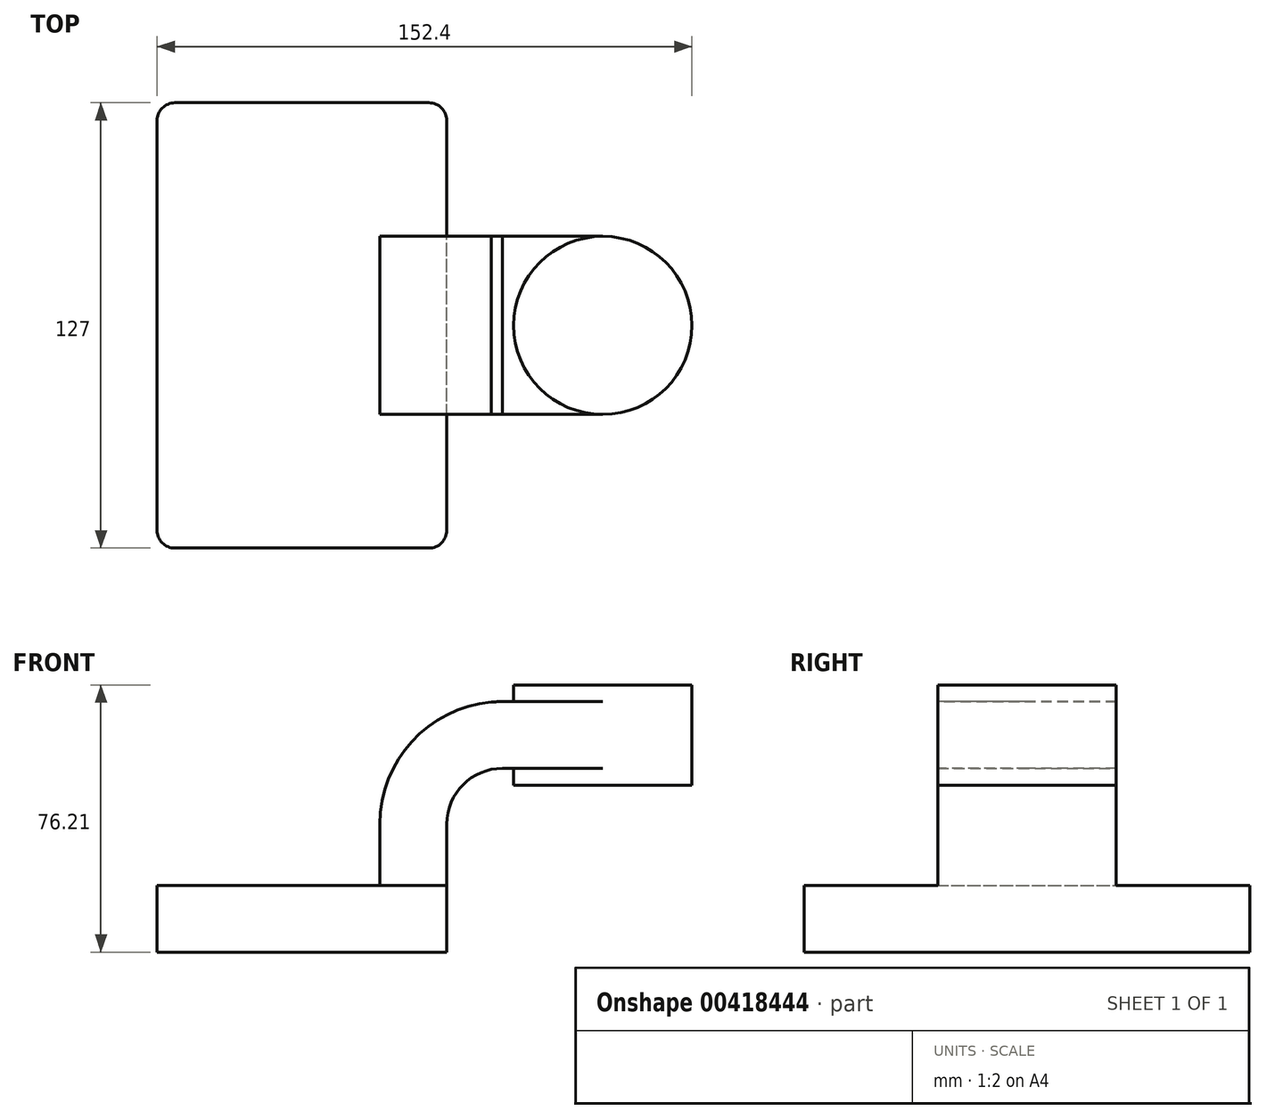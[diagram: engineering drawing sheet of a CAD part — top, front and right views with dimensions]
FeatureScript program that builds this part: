
annotation { "Feature Type Name" : "Feature", "Feature Type Description" : "" }
export const myFeature = defineFeature(function(context is Context, id is Id, definition is map)
    precondition{}
    {
        {
            var Q0;
            Q0=qCreatedBy(makeId("Front.planeOp"),FACE);
            var sketch = newSketch(context, id + "F0", { "sketchPlane" : qUnion([Q0])});
            skLineSegment(sketch, "E0.rect.bottom", {"start": v(-41.28, 9.52) * mm, "end": v(41.28, 9.52) * mm});
            skLineSegment(sketch, "E0.rect.top", {"start": v(-41.28, -9.52) * mm, "end": v(41.28, -9.52) * mm});
            skLineSegment(sketch, "E0.rect.left", {"start": v(-41.28, 9.52) * mm, "end": v(-41.28, -9.52) * mm});
            skLineSegment(sketch, "E0.rect.right", {"start": v(41.28, 9.52) * mm, "end": v(41.28, -9.52) * mm});
            skPoint(sketch, "E0.rect.middle", {"position": v(0, 0) * mm});
            skLineSegment(sketch, "E1", {"start": v(41.28, 9.52) * mm, "end": v(41.28, 27) * mm});
            skArc(sketch, "E2", {"start": v(41.28, 27) * mm, "mid": v(45.92, 38.23) * mm, "end": v(57.15, 42.88) * mm});
            skLineSegment(sketch, "E3", {"start": v(57.15, 42.88) * mm, "end": v(85.72, 42.88) * mm});
            skLineSegment(sketch, "E4.rect.bottom", {"start": v(60.32, 38.1) * mm, "end": v(111.12, 38.1) * mm});
            skLineSegment(sketch, "E4.rect.top", {"start": v(60.32, 66.68) * mm, "end": v(111.12, 66.68) * mm});
            skLineSegment(sketch, "E4.rect.left", {"start": v(60.32, 38.1) * mm, "end": v(60.32, 66.68) * mm});
            skLineSegment(sketch, "E4.rect.right", {"start": v(111.13, 38.1) * mm, "end": v(111.12, 66.68) * mm});
            skPoint(sketch, "E4.rect.middle", {"position": v(85.72, 52.39) * mm});
            skLineSegment(sketch, "E5.0", {"start": v(57.15, 61.93) * mm, "end": v(85.72, 61.93) * mm});
            skArc(sketch, "E5.1", {"start": v(22.23, 27) * mm, "mid": v(32.45, 51.7) * mm, "end": v(57.15, 61.93) * mm});
            skLineSegment(sketch, "E5.2", {"start": v(22.23, 9.52) * mm, "end": v(22.23, 27) * mm});
            skLineSegment(sketch, "E6", {"start": v(85.72, 38.1) * mm, "end": v(85.72, 66.68) * mm});
            skFitSpline(sketch, "E7", {"points": [v(-41.28, 9.53) * mm, v(57.15, 61.93) * mm], "startDerivative": vector(5.2, 92.34) * mm, "endDerivative": vector(120.92, 4.22) * mm});
            skSolve(sketch);
        }
        {
            var Q0;
            Q0=makeQuery(id+"F0.imprint","IMPRINT",FACE,{"disambiguationData":[TD([[makeQuery(id+"F0.imprint","IMPRINT",EDGE,{"derivedFrom":sQuery(id+"F0.wireOp",EDGE,"E0.rect.top")}),1.0]])]});
            extrude(context, id + "F1", {"entities" : qUnion([Q0]), "endBound" : BoundingType.SYMMETRIC, "depth" : 127 * mm});
        }
        {
            var Q0;
            {var subQ9=sQuery(id+"F0.wireOp",EDGE,"E1");Q0=makeQuery(id+"F0.imprint","IMPRINT",FACE,{"disambiguationData":[TD([[makeQuery(id+"F0.imprint","IMPRINT",EDGE,{"derivedFrom":subQ9}),1.0]])]});}
            var Q1;
            {var subQ0=sQuery(id+"F0.wireOp",EDGE,"E6");var subQ1=sQuery(id+"F0.wireOp",EDGE,"E3");var subQ2=makeQuery(id+"F0.imprint","INTERSECT",VERTEX,{"derivedFrom":[subQ1,subQ0]});Q1=makeQuery(id+"F0.imprint","IMPRINT",FACE,{"disambiguationData":[TD([[makeQuery(id+"F0.imprint","IMPRINT",EDGE,{"disambiguationData":[TD([[subQ2,1.0]])],"derivedFrom":subQ1}),1.0]])]});}
            extrude(context, id + "F2", {"entities" : qUnion([Q0, Q1]), "operationType" : NewBodyOperationType.ADD, "endBound" : BoundingType.SYMMETRIC, "depth" : 50.8 * mm});
        }
        {
            var Q0;
            {var subQ3=sQuery(id+"F0.wireOp",EDGE,"E5.2");Q0=makeQuery(id+"F0.imprint","IMPRINT",FACE,{"disambiguationData":[TD([[makeQuery(id+"F0.imprint","IMPRINT",EDGE,{"derivedFrom":subQ3}),1.0]])]});}
            extrude(context, id + "F3", {"entities" : qUnion([Q0]), "operationType" : NewBodyOperationType.ADD, "endBound" : BoundingType.SYMMETRIC, "depth" : 15.88 * mm});
        }
        {
            var Q0;
            {var subQ5=sQuery(id+"F0.wireOp",EDGE,"E4.rect.right");Q0=makeQuery(id+"F0.imprint","IMPRINT",FACE,{"disambiguationData":[TD([[makeQuery(id+"F0.imprint","IMPRINT",EDGE,{"derivedFrom":subQ5}),1.0]])]});}
            var Q1;
            Q1=sQuery(id+"F0.wireOp",EDGE,"E6");
            revolve(context, id + "F4", {"operationType" : NewBodyOperationType.ADD, "entities" : qUnion([Q0]), "axis" : qUnion([Q1]), "revolveType" : RevolveType.FULL});
        }
        {
            var Q0;
            Q0=makeQuery(id+"F1.opExtrude","CAP_EDGE",EDGE,{"disambiguationData":[OSD([sQuery(id+"F0.wireOp",EDGE,"E0.rect.right")])],"isStart":false});
            var Q1;
            Q1=makeQuery(id+"F1.opExtrude","CAP_EDGE",EDGE,{"disambiguationData":[OSD([sQuery(id+"F0.wireOp",EDGE,"E0.rect.left")])],"isStart":false});
            var Q2;
            Q2=makeQuery(id+"F1.opExtrude","CAP_EDGE",EDGE,{"disambiguationData":[OSD([sQuery(id+"F0.wireOp",EDGE,"E0.rect.right")])],"isStart":true});
            var Q3;
            Q3=makeQuery(id+"F1.opExtrude","CAP_EDGE",EDGE,{"disambiguationData":[OSD([sQuery(id+"F0.wireOp",EDGE,"E0.rect.left")])],"isStart":true});
            fillet(context, id + "F5", {"entities" : qUnion([Q0, Q1, Q2, Q3]), "radius" : 5.08 * mm, "tangentPropagation" : true, "allowEdgeOverflow" : false});
        }
        {
            var Q0;
            Q0=makeQuery(id+"F3.opExtrude","CAP_FACE",FACE,{"disambiguationData":[OSD([sQuery(id+"F0.wireOp",EDGE,"E0.rect.bottom"),sQuery(id+"F0.wireOp",EDGE,"E5.1"),sQuery(id+"F0.wireOp",EDGE,"E5.2"),sQuery(id+"F0.wireOp",EDGE,"E7")])],"isStart":false});
            extrude(context, id + "F6", {"entities" : qUnion([Q0]), "operationType" : NewBodyOperationType.REMOVE, "endBound" : BoundingType.SYMMETRIC, "depth" : 76.2 * mm});
        }
    });
